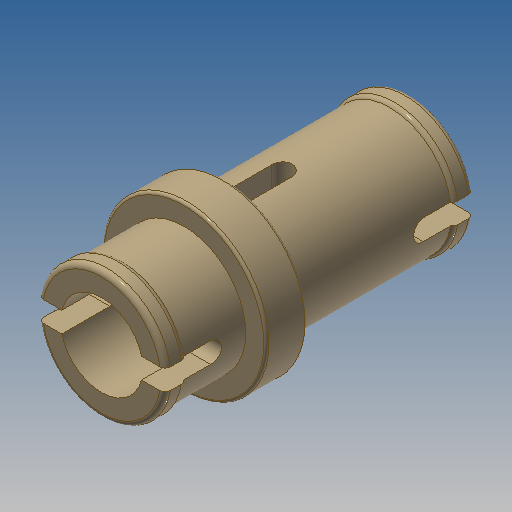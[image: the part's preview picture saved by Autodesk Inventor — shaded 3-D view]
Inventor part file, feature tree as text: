
AUTODESK INVENTOR PART (.ipt)
format: ipt  version: 2022.2 (Build 262287000, 287)  size: 297,984 bytes
history: native  units: mm (DEFAULTED — no unit token found)
features: sketch x2, extrude x2, revolve x1, fillet x1
ambient origin geometry x8: Origin, YZ Plane, XZ Plane, XY Plane, X Axis, Y Axis, Z Axis, Center Point
bodies: Solid2 (feature_tree)
feature tree (6):
  sketch  "Sketch1"  dims[d1=4.8mm d2=5.0mm d6=4.0mm]
  revolve  "Revolution1"  [1 undecoded]
  fillet  "Fillet1"  Radius=4.0mm
  extrude  "Extrusion1"  Depth=0.8mm
  extrude  "Extrusion2"  Depth=0.8mm
  sketch  "Sketch2"  dims[d7=0.8mm d8=6.4mm d9=0.8mm d10=0.8mm d19=8.0mm d20=90.0deg d21=4.8mm d22=0.0mm d24=0.8mm d25=10.0mm d26=0.0mm d27=0.2mm d28=0.1mm d29=0.0mm d30=0.0mm d31=2.266667mm d33=3.4mm d34=3.2mm d35=0.8mm]
note: 1 required parameter value undecoded (feature->parameter linkage not recoverable at this tier; creation-order binding heuristic only, values carry confidence <= 0.55)
